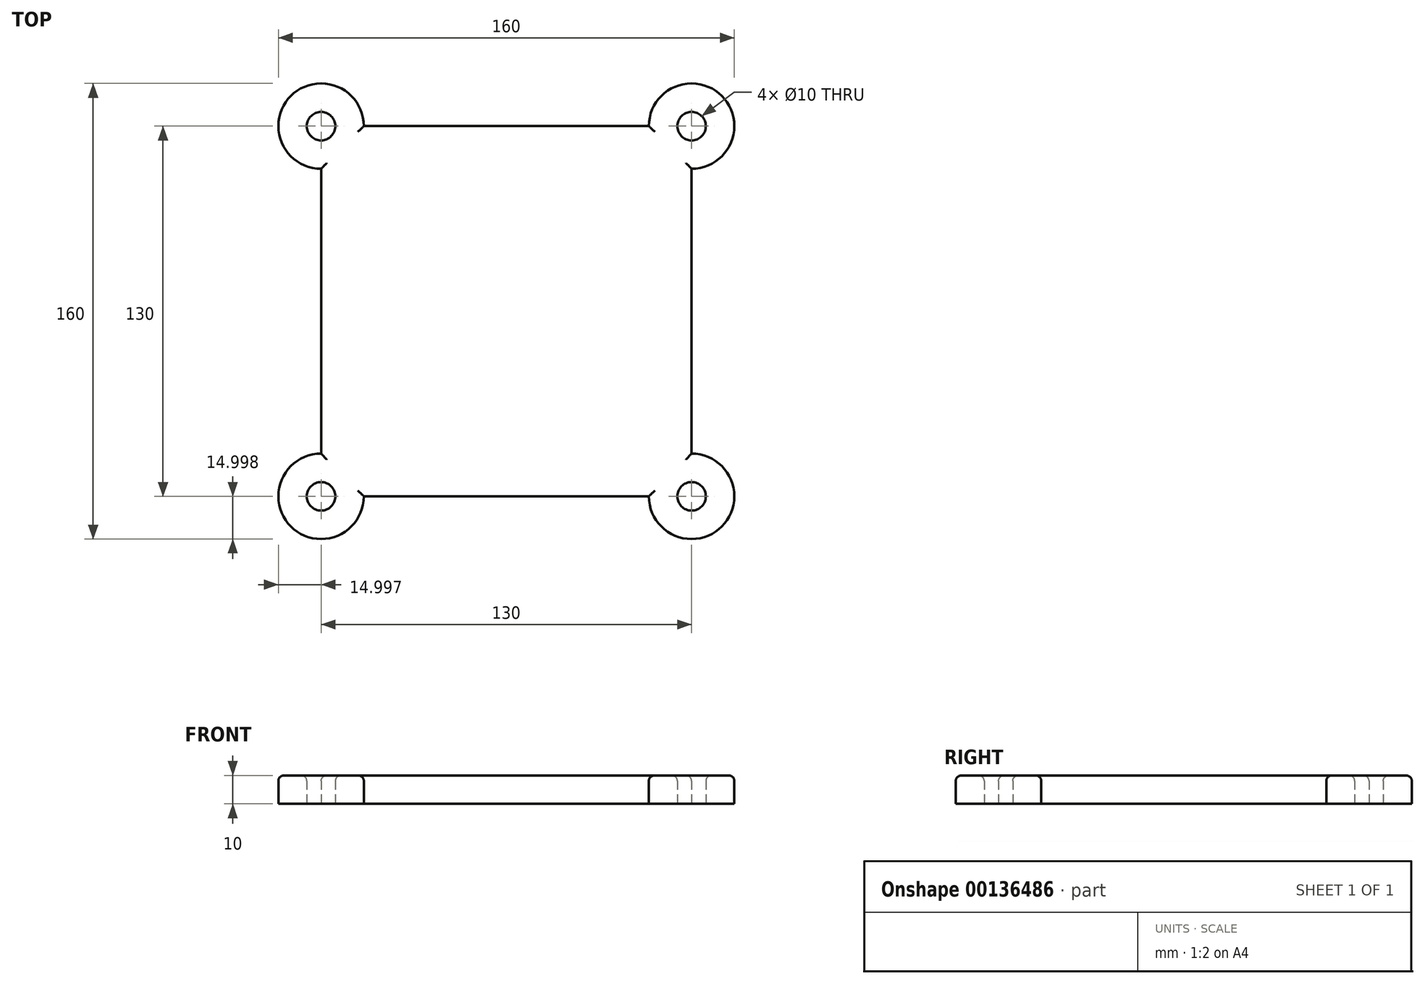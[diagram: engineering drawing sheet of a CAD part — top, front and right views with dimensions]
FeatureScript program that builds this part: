
annotation { "Feature Type Name" : "Feature", "Feature Type Description" : "" }
export const myFeature = defineFeature(function(context is Context, id is Id, definition is map)
    precondition{}
    {
        {
            var Q0;
            Q0=qCreatedBy(makeId("Top.planeOp"),FACE);
            var sketch = newSketch(context, id + "F0", { "sketchPlane" : qUnion([Q0])});
            skArc(sketch, "E0", {"start": v(-65.6, 65.7) * mm, "mid": v(-91.2, 76.31) * mm, "end": v(-80.6, 50.7) * mm});
            skArc(sketch, "E1", {"start": v(49.4, 50.7) * mm, "mid": v(60, 76.31) * mm, "end": v(34.4, 65.7) * mm});
            skArc(sketch, "E2", {"start": v(-80.6, -49.3) * mm, "mid": v(-91.2, -74.9) * mm, "end": v(-65.6, -64.3) * mm});
            skArc(sketch, "E3", {"start": v(34.4, -64.3) * mm, "mid": v(60, -74.9) * mm, "end": v(49.4, -49.3) * mm});
            skLineSegment(sketch, "E4", {"start": v(-65.6, 65.7) * mm, "end": v(34.4, 65.7) * mm});
            skLineSegment(sketch, "E5", {"start": v(49.4, -49.3) * mm, "end": v(49.4, 50.7) * mm});
            skLineSegment(sketch, "E6", {"start": v(34.4, -64.3) * mm, "end": v(-65.6, -64.3) * mm});
            skLineSegment(sketch, "E7", {"start": v(-80.6, -49.3) * mm, "end": v(-80.6, 50.7) * mm});
            skCircle(sketch, "E8", {"center": v(-80.6, 65.7) * mm, "radius": 5 * mm});
            skCircle(sketch, "E9", {"center": v(49.4, 65.7) * mm, "radius": 5 * mm});
            skCircle(sketch, "E10", {"center": v(49.4, -64.3) * mm, "radius": 5 * mm});
            skCircle(sketch, "E11", {"center": v(-80.6, -64.3) * mm, "radius": 5 * mm});
            skSolve(sketch);
        }
        {
            var Q0;
            Q0=makeQuery(id+"F0.imprint","IMPRINT",FACE,{"disambiguationData":[TD([[makeQuery(id+"F0.imprint","IMPRINT",EDGE,{"derivedFrom":sQuery(id+"F0.wireOp",EDGE,"E0")}),1.0]])]});
            extrude(context, id + "F1", {"entities" : qUnion([Q0]), "depth" : 10 * mm});
        }
        {
            var Q0;
            Q0=makeQuery(id+"F1.opExtrude","CAP_FACE",FACE,{"disambiguationData":[OSD([sQuery(id+"F0.wireOp",EDGE,"E0"),sQuery(id+"F0.wireOp",EDGE,"E1"),sQuery(id+"F0.wireOp",EDGE,"E2"),sQuery(id+"F0.wireOp",EDGE,"E3"),sQuery(id+"F0.wireOp",EDGE,"E4"),sQuery(id+"F0.wireOp",EDGE,"E5"),sQuery(id+"F0.wireOp",EDGE,"E6"),sQuery(id+"F0.wireOp",EDGE,"E7"),sQuery(id+"F0.wireOp",EDGE,"E8"),sQuery(id+"F0.wireOp",EDGE,"E9"),sQuery(id+"F0.wireOp",EDGE,"E10"),sQuery(id+"F0.wireOp",EDGE,"E11")])],"isStart":false});
            fillet(context, id + "F2", {"entities" : qUnion([Q0]), "radius" : 2 * mm, "tangentPropagation" : true, "allowEdgeOverflow" : false});
        }
    });
